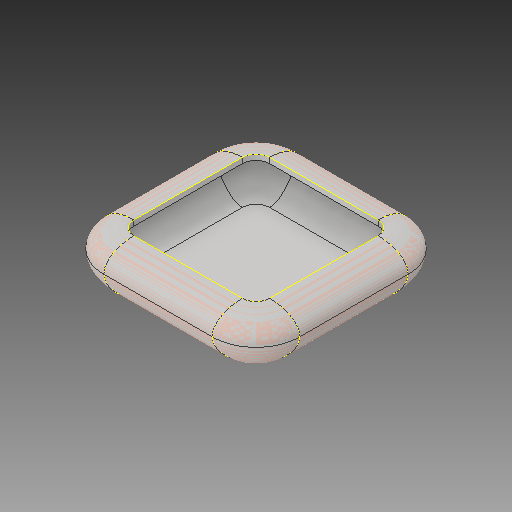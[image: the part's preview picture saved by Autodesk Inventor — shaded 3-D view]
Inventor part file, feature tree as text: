
AUTODESK INVENTOR PART (.ipt)
format: ipt  version: 2018 (Build 220112000, 112)  size: 409,088 bytes
history: native  units: in
note: dims shown in document units (in); Inventor stores cm internally (conversion verified against a paired STEP export)
features: other x4, sketch x3, plane x3, thicken_offset x2, split x1, sweep x1, surface_op x1
ambient origin geometry x8: Origin, YZ Plane, XZ Plane, XY Plane, X Axis, Y Axis, Z Axis, Center Point
bodies: Solid1 (feature_tree)
feature tree (15):
  sketch  "Sketch1"  dims[d0=1.25in d1=1.25in]
  plane  "Work Plane1"
  sketch  "Sketch2"  dims[d2=0.126in]
  plane  "Work Plane2"
  thicken_offset  "Thicken1"
  thicken_offset  "Thicken2"
  plane  "Work Plane3"
  split  "Split1"
  sketch  "Sketch4"  dims[d3=0.45in d4=1.25in d5=1.25in d6=0.126in d7=0.275in d8=0.0in d9=0.0in d10=0.05in d11=0.05in d12=0.05in d13=0.05in d14=0.28in d15=0.15in]
  other  "Srf1"
  other  "Srf2"
  sweep  "SweepSrf1"
  other  "Top Solid"
  other  "Bottom Solid"
  surface_op  "Boundary Patch1"
